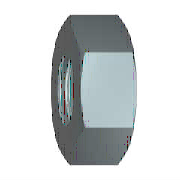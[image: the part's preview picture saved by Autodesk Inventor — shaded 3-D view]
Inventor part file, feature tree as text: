
AUTODESK INVENTOR PART (.ipt)
format: ipt  version: 2022 (Build 260153000, 153)  size: 164,864 bytes
history: native  units: mm (DEFAULTED — no unit token found)
features: sketch x3, other x2, extrude x1, hole x1, plane x1
ambient origin geometry x7: Origin, YZ Plane, XZ Plane, X Axis, Y Axis, Z Axis, Center Point
bodies: Solid1 (feature_tree)
feature tree (8):
  extrude  "Базовый элемент"  Depth=8.082904mm
  other  "Фаска1"
  hole  "Резьба"  [1 undecoded]
  other  "Work Axis1"
  plane  "Work Plane1"
  sketch  "Эскиз1"
  sketch  "Эскиз2"
  sketch  "Эскиз3"
note: 1 required parameter value undecoded (feature->parameter linkage not recoverable at this tier; creation-order binding heuristic only, values carry confidence <= 0.55)
